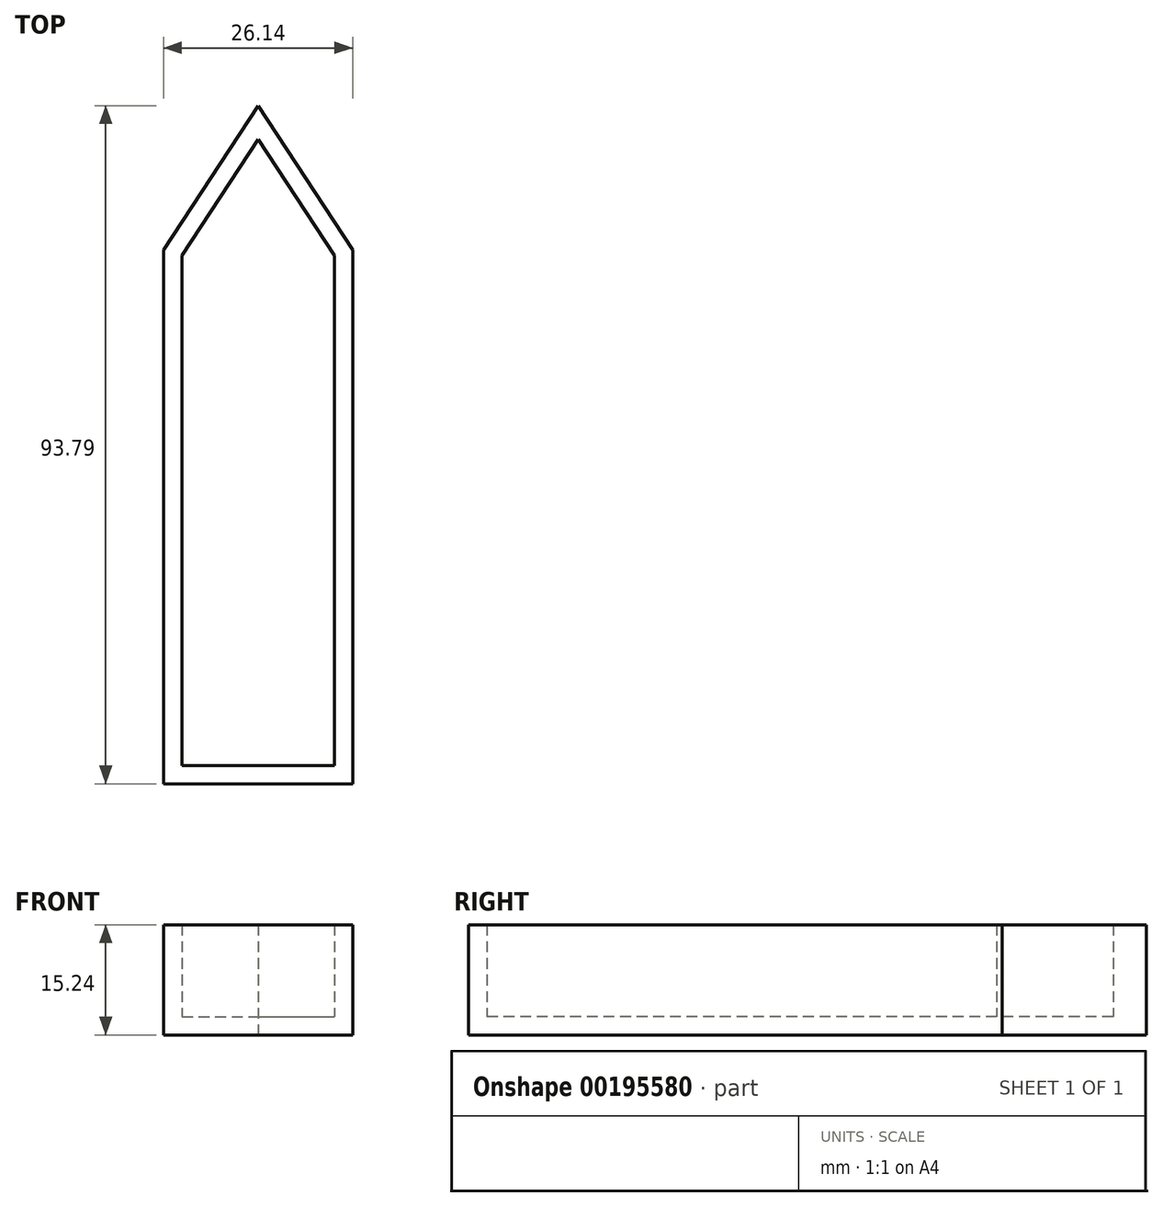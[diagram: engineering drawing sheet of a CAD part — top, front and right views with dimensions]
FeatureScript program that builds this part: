
annotation { "Feature Type Name" : "Feature", "Feature Type Description" : "" }
export const myFeature = defineFeature(function(context is Context, id is Id, definition is map)
    precondition{}
    {
        {
            var Q0;
            Q0=qCreatedBy(makeId("Top.planeOp"),FACE);
            var sketch = newSketch(context, id + "F0", { "sketchPlane" : qUnion([Q0])});
            skLineSegment(sketch, "E0.bottom", {"start": v(-26.14, 52.45) * mm, "end": v(0, 52.45) * mm});
            skLineSegment(sketch, "E0.top", {"start": v(-26.14, -21.39) * mm, "end": v(0, -21.39) * mm});
            skLineSegment(sketch, "E0.left", {"start": v(-26.14, 52.45) * mm, "end": v(-26.14, -21.39) * mm});
            skLineSegment(sketch, "E0.right", {"start": v(0, 52.45) * mm, "end": v(0, -21.39) * mm});
            skLineSegment(sketch, "E1", {"start": v(-26.14, 52.45) * mm, "end": v(-13.07, 72.4) * mm});
            skPoint(sketch, "E1.endSnap0", {"position": v(-13.07, 52.45) * mm});
            skLineSegment(sketch, "E2", {"start": v(-13.07, 72.4) * mm, "end": v(0, 52.45) * mm});
            skSolve(sketch);
        }
        {
            var Q0;
            Q0=makeQuery(id+"F0.imprint","IMPRINT",FACE,{"disambiguationData":[TD([[makeQuery(id+"F0.imprint","IMPRINT",EDGE,{"derivedFrom":sQuery(id+"F0.wireOp",EDGE,"E0.bottom")}),-1.0]])]});
            var Q1;
            Q1=makeQuery(id+"F0.imprint","IMPRINT",FACE,{"disambiguationData":[TD([[makeQuery(id+"F0.imprint","IMPRINT",EDGE,{"derivedFrom":sQuery(id+"F0.wireOp",EDGE,"E0.bottom")}),1.0]])]});
            extrude(context, id + "F1", {"entities" : qUnion([Q0, Q1]), "depth" : 15.24 * mm});
        }
        {
            var Q0;
            Q0=makeQuery(id+"F1.opExtrude","CAP_FACE",FACE,{"disambiguationData":[OSD([sQuery(id+"F0.wireOp",EDGE,"E0.top"),sQuery(id+"F0.wireOp",EDGE,"E0.left"),sQuery(id+"F0.wireOp",EDGE,"E0.right"),sQuery(id+"F0.wireOp",EDGE,"E1"),sQuery(id+"F0.wireOp",EDGE,"E2")])],"isStart":false});
            shell(context, id + "F2", {"entities" : qUnion([Q0]), "thickness" : 2.54 * mm});
        }
    });
